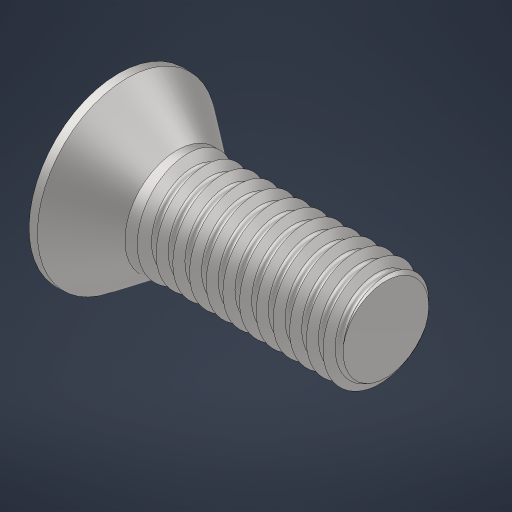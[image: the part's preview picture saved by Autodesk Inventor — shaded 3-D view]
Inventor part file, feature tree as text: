
AUTODESK INVENTOR PART (.ipt)
format: ipt  version: 2024 (Build 280153000, 153)  size: 578,560 bytes
history: native  units: mm
features: sketch x7, other x4, revolve x3, extrude x3, chamfer x2
ambient origin geometry x8: Origin, YZ Plane, XZ Plane, XY Plane, X Axis, Y Axis, Z Axis, Center Point
bodies: Body1 (feature_tree)
feature tree (19):
  other  "솔리드1"
  revolve  "회전1"
  other  "코일2"
  extrude  "돌출2"  Depth=2.8mm
  revolve  "회전2"
  sketch  "스케치9"
  extrude  "돌출3"  Depth=10.0mm
  revolve  "회전3"
  chamfer  "모따기1"  Distance=9.6mm
  chamfer  "모따기2"  Distance=5.0mm
  extrude  "돌출4"  TaperAngle=90.0deg  [1 undecoded]
  sketch  "스케치1"
  sketch  "스케치3"
  sketch  "스케치7"
  sketch  "스케치8"
  sketch  "스케치11"
  sketch  "스케치12"
  other  "Finish1"
  other  "Finish2"
note: 1 required parameter value undecoded (feature->parameter linkage not recoverable at this tier; creation-order binding heuristic only, values carry confidence <= 0.55)
